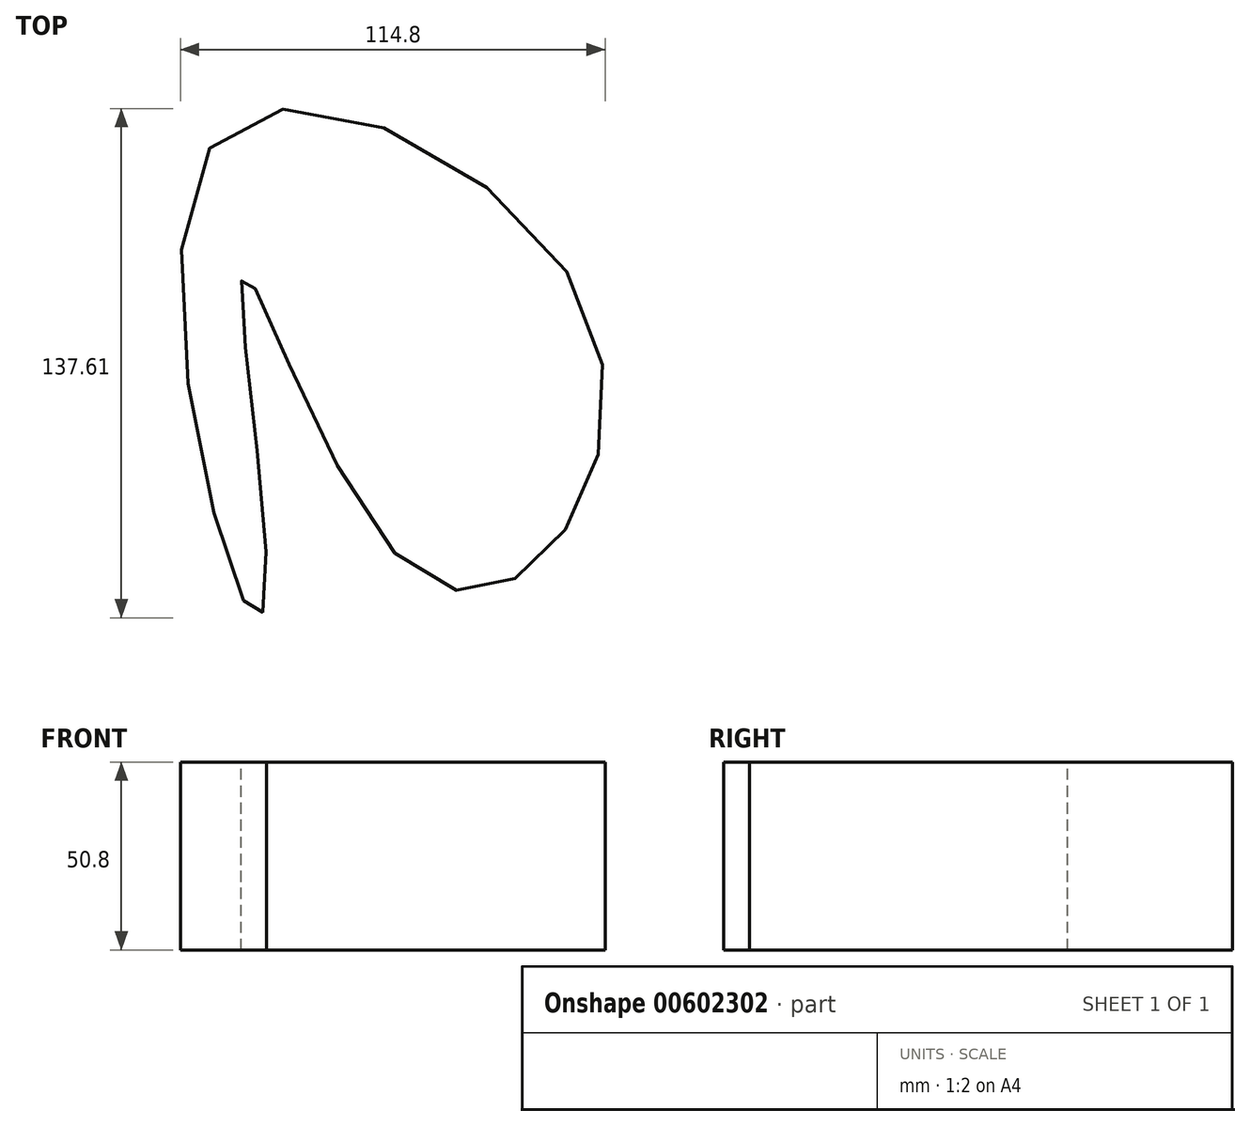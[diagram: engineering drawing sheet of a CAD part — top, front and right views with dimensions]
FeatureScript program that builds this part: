
annotation { "Feature Type Name" : "Feature", "Feature Type Description" : "" }
export const myFeature = defineFeature(function(context is Context, id is Id, definition is map)
    precondition{}
    {
        {
            var Q0;
            Q0=qCreatedBy(makeId("Top.planeOp"),FACE);
            var sketch = newSketch(context, id + "F0", { "sketchPlane" : qUnion([Q0])});
            skFitSpline(sketch, "E0", {"points": [v(-48.96, -51.5) * mm, v(-54.8, 23.63) * mm, v(-12.92, -53.1) * mm, v(25.82, -53.02) * mm, v(33.3, 22.68) * mm, v(-63.09, 59.12) * mm, v(-52.63, -68.52) * mm, v(-48.96, -51.5) * mm]});
            skSolve(sketch);
        }
        {
            var Q0;
            Q0=makeQuery(id+"F0.imprint","IMPRINT",FACE,{"disambiguationData":[TD([[makeQuery(id+"F0.imprint","IMPRINT",EDGE,{"derivedFrom":sQuery(id+"F0.wireOp",EDGE,"E0")}),1.0]])]});
            var Q1;
            Q1=sQuery(id+"F0.wireOp",EDGE,"E0");
            extrude(context, id + "F1", {"entities" : qUnion([Q0]), "surfaceEntities" : qUnion([Q1]), "oppositeDirection" : true, "depth" : 50.8 * mm, "offsetDistance" : 25.4 * mm});
        }
    });
